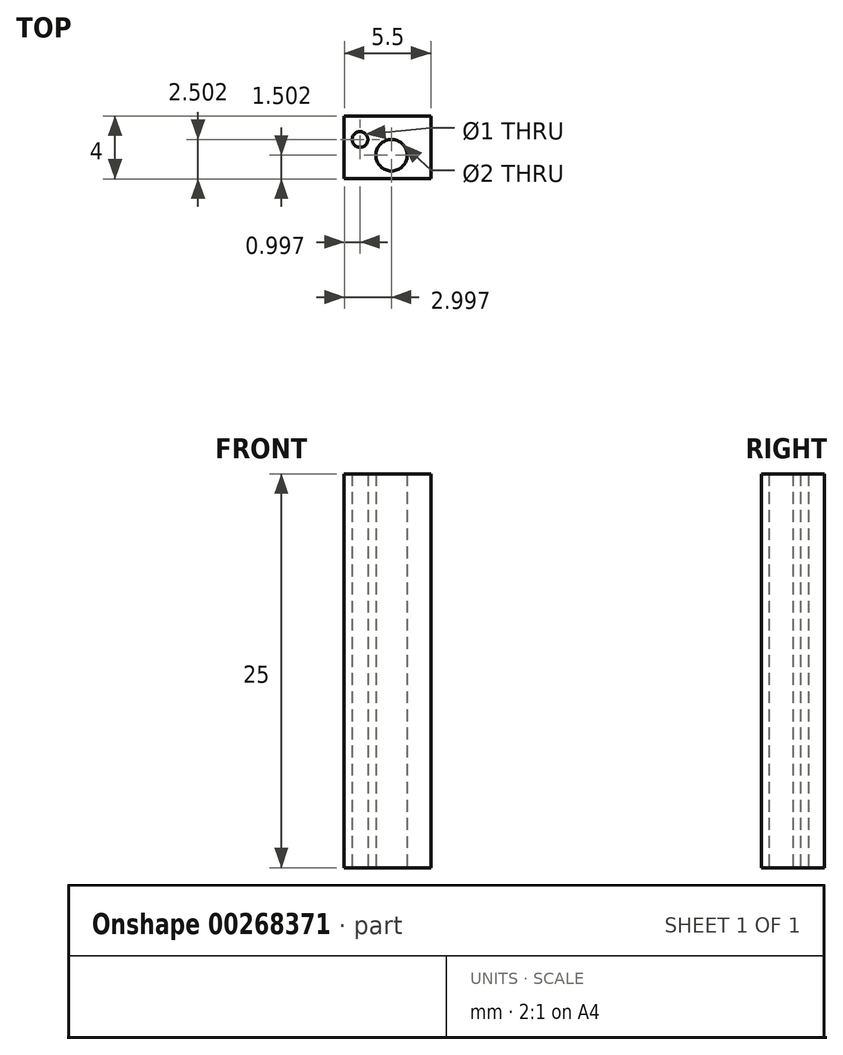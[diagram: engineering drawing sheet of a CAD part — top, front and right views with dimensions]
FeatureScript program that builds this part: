
annotation { "Feature Type Name" : "Feature", "Feature Type Description" : "" }
export const myFeature = defineFeature(function(context is Context, id is Id, definition is map)
    precondition{}
    {
        {
            var Q0;
            Q0=qCreatedBy(makeId("Top.planeOp"),FACE);
            var sketch = newSketch(context, id + "F0", { "sketchPlane" : qUnion([Q0])});
            skLineSegment(sketch, "E0", {"start": v(-53.68, 37.61) * mm, "end": v(-48.18, 37.61) * mm});
            skLineSegment(sketch, "E1", {"start": v(-48.18, 37.61) * mm, "end": v(-48.18, 33.61) * mm});
            skLineSegment(sketch, "E2", {"start": v(-48.18, 33.61) * mm, "end": v(-53.68, 33.61) * mm});
            skLineSegment(sketch, "E3", {"start": v(-53.68, 33.61) * mm, "end": v(-53.68, 37.61) * mm});
            skLineSegment(sketch, "E4", {"start": v(-48.18, 33.61) * mm, "end": v(-48.18, 35.11) * mm});
            skLineSegment(sketch, "E5", {"start": v(-53.68, 33.61) * mm, "end": v(-50.68, 33.61) * mm});
            skLineSegment(sketch, "E6", {"start": v(-50.68, 33.61) * mm, "end": v(-50.68, 35.11) * mm, "construction": true});
            skCircle(sketch, "E7", {"center": v(-50.68, 35.11) * mm, "radius": 0.5 * mm});
            skCircle(sketch, "E8", {"center": v(-50.68, 35.11) * mm, "radius": 1 * mm});
            skLineSegment(sketch, "E9", {"start": v(-53.68, 37.61) * mm, "end": v(-52.68, 37.61) * mm});
            skLineSegment(sketch, "E10", {"start": v(-53.68, 33.61) * mm, "end": v(-53.68, 36.11) * mm});
            skLineSegment(sketch, "E11", {"start": v(-53.68, 36.11) * mm, "end": v(-52.68, 36.11) * mm});
            skCircle(sketch, "E12", {"center": v(-52.68, 36.11) * mm, "radius": 0.5 * mm});
            skLineSegment(sketch, "E13", {"start": v(-48.18, 37.61) * mm, "end": v(-48.18, 35.61) * mm});
            skLineSegment(sketch, "E14", {"start": v(-48.18, 35.61) * mm, "end": v(-49.34, 37.61) * mm});
            skSolve(sketch);
        }
        {
            var Q0;
            Q0 = qSketchRegion(id + "F0", true);
            extrude(context, id + "F1", {"entities" : qUnion([Q0]), "depth" : 25 * mm});
        }
    });
